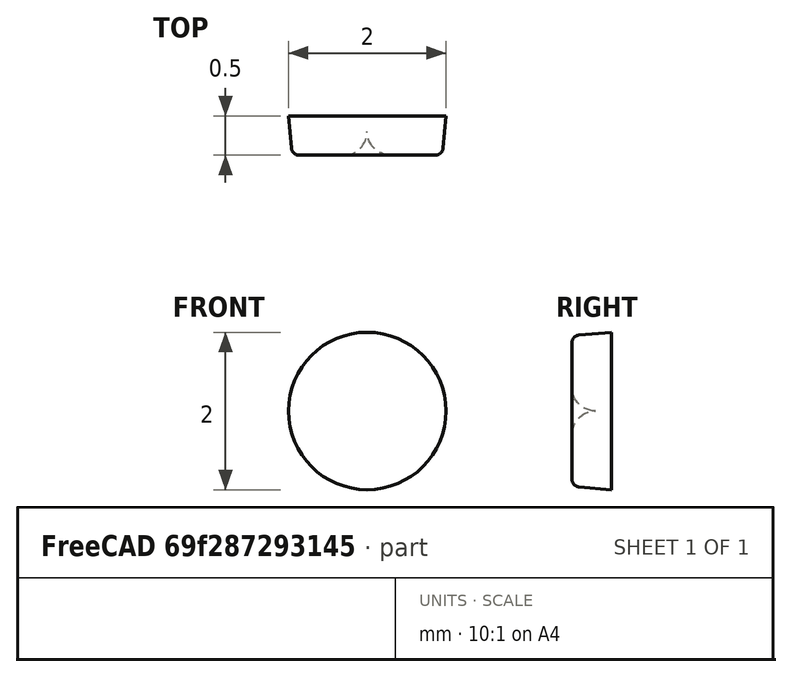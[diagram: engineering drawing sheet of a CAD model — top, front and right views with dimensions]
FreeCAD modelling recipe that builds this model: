
FCSTD DOCUMENT  (FreeCAD 0.16R6712 (Git))
Label: rubberfoot
License: All rights reserved
LicenseURL: http://en.wikipedia.org/wiki/All_rights_reserved
objects: Sketcher::SketchObject×1, PartDesign::Revolution×1, Mesh::Feature×1
note: 3 computed .brp shape members not serialized (recipe doc carries the construction recipe); baked Part::Feature solids carry a one-line shape summary decoded from their .brp

FEATURE [Sketcher::SketchObject] Sketch
  sketch-geometry (6):
    g0: LineSegment StartX=-1 StartY=0 StartZ=0 EndX=-0.964242 EndY=-0.408716 EndZ=0
    g1: LineSegment StartX=-0.864623 StartY=-0.5 StartZ=0 EndX=-0.3 EndY=-0.5 EndZ=0
    g2: ArcOfCircle CenterX=-0.864623 CenterY=-0.4 CenterZ=0 NormalX=0 NormalY=0 NormalZ=1 Radius=0.1 StartAngle=3.22886 EndAngle=4.71239
    g3: LineSegment StartX=0 StartY=-0.2 StartZ=0 EndX=0 EndY=0 EndZ=0
    g4: LineSegment StartX=-1 StartY=0 StartZ=0 EndX=0 EndY=0 EndZ=0
    g5: ArcOfCircle CenterX=-0.3 CenterY=-0.2 CenterZ=0 NormalX=0 NormalY=0 NormalZ=1 Radius=0.3 StartAngle=4.71239 EndAngle=6.28319
  constraints (18):
    c: Horizontal(g1)
    c: Vertical(g3)
    c: Horizontal(g4)
    c: Coincident(g2,g1)
    c: Coincident(g2,g0)
    c: Coincident(g4,g3)
    c: PointOnObject(g-1,g4)
    c: Tangent(g0,g2)
    c: Tangent(g1,g2)
    c: Coincident(g4,g0)
    c: Angle(g0,g-2) = 3.05433
    c: DistanceY(g-1,g1) = -0.5
    c: Coincident(g3,g-1)
    c: DistanceX(g-2,g0) = -1
    c: Radius(g2) = 0.1
    c: Tangent(g3,g5) = -1.5708
    c: Tangent(g1,g5) = -1.5708
    c: Radius(g5) = 0.3
FEATURE [PartDesign::Revolution] Revolution
  Angle = 360
  Axis = (0,1,0)
  Base = (0,0,0)
  ReferenceAxis = -> Sketch [V_Axis]
  Sketch = -> Sketch
FEATURE [Mesh::Feature] Mesh  label="Revolution (Meshed)"
